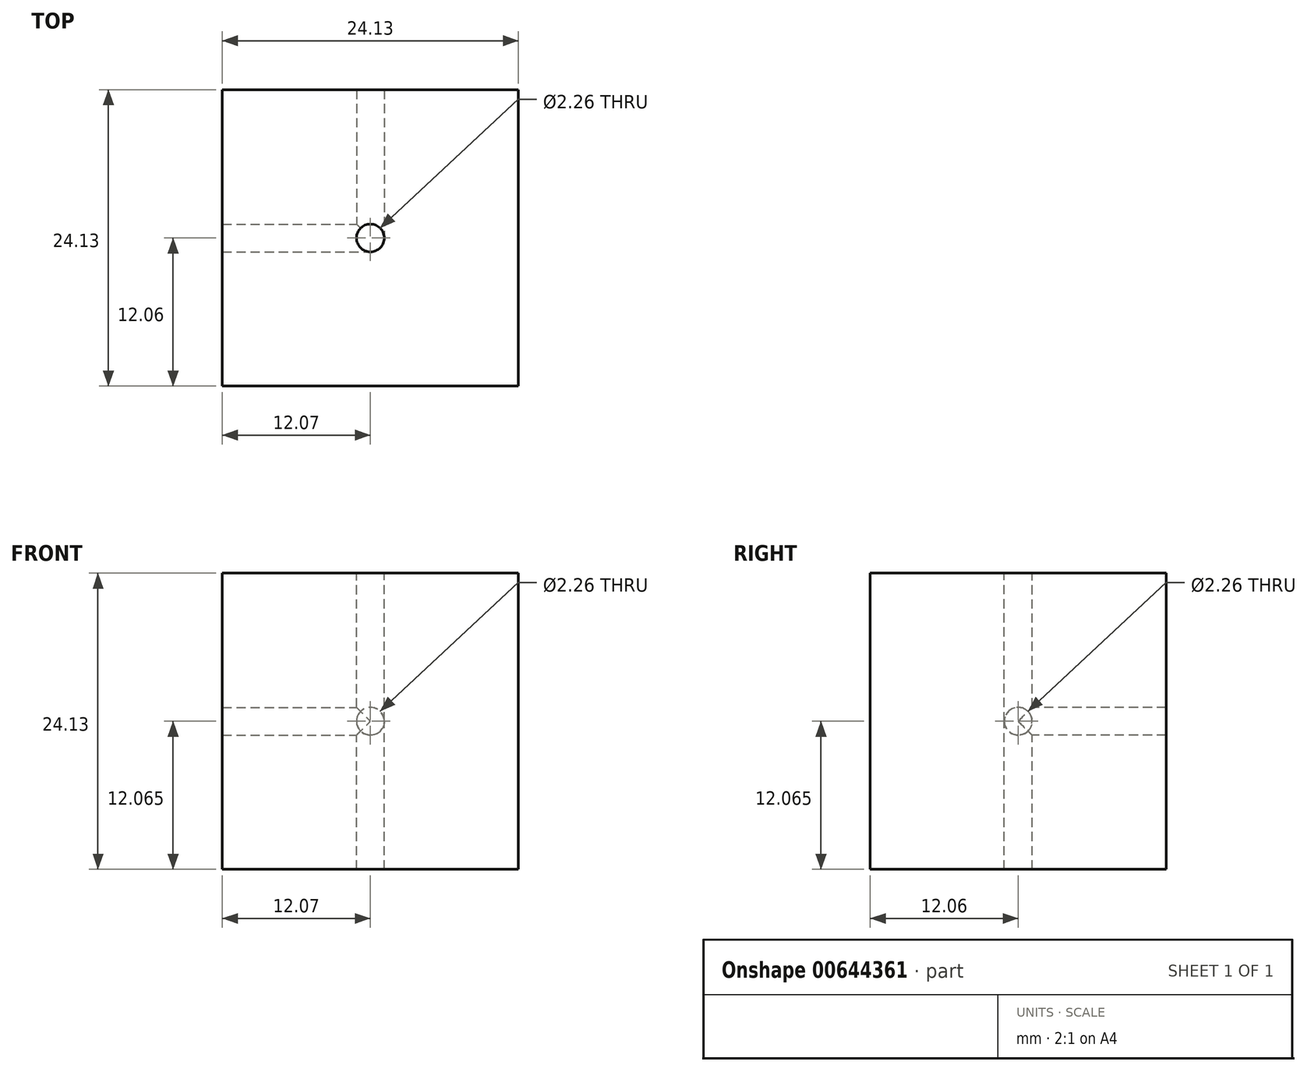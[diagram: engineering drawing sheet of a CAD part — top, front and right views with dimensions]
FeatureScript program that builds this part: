
annotation { "Feature Type Name" : "Feature", "Feature Type Description" : "" }
export const myFeature = defineFeature(function(context is Context, id is Id, definition is map)
    precondition{}
    {
        {
            var Q0;
            Q0=qCreatedBy(makeId("Top.planeOp"),FACE);
            var sketch = newSketch(context, id + "F0", { "sketchPlane" : qUnion([Q0])});
            skLineSegment(sketch, "E0.bottom", {"start": v(12.07, 12.07) * mm, "end": v(-12.07, 12.07) * mm});
            skLineSegment(sketch, "E0.top", {"start": v(12.07, -12.06) * mm, "end": v(-12.07, -12.06) * mm});
            skLineSegment(sketch, "E0.left", {"start": v(12.07, 12.07) * mm, "end": v(12.07, -12.06) * mm});
            skLineSegment(sketch, "E0.right", {"start": v(-12.07, 12.07) * mm, "end": v(-12.07, -12.06) * mm});
            skPoint(sketch, "E0.middle", {"position": v(0, 0) * mm});
            skSolve(sketch);
        }
        {
            var Q0;
            Q0=makeQuery(id+"F0.imprint","IMPRINT",FACE,{"disambiguationData":[TD([[makeQuery(id+"F0.imprint","IMPRINT",EDGE,{"derivedFrom":sQuery(id+"F0.wireOp",EDGE,"E0.bottom")}),1.0]])]});
            extrude(context, id + "F1", {"entities" : qUnion([Q0]), "depth" : 24.13 * mm, "offsetDistance" : 25.4 * mm});
        }
        {
            var Q0;
            Q0=makeQuery(id+"F1.opExtrude","CAP_FACE",FACE,{"disambiguationData":[OSD([sQuery(id+"F0.wireOp",EDGE,"E0.bottom"),sQuery(id+"F0.wireOp",EDGE,"E0.top"),sQuery(id+"F0.wireOp",EDGE,"E0.left"),sQuery(id+"F0.wireOp",EDGE,"E0.right")])],"isStart":false});
            var sketch = newSketch(context, id + "F2", { "sketchPlane" : qUnion([Q0])});
            skPoint(sketch, "E1", {"position": v(0, 0) * mm});
            skSolve(sketch);
        }
        {
            var Q0;
            Q0=sQuery(id+"F2.wireOp",VERTEX,"E1");
            var Q1;
            Q1=makeQuery(id+"F1.opExtrude","SWEPT_BODY",BODY,{"disambiguationData":[OSD([sQuery(id+"F0.wireOp",EDGE,"E0.bottom"),sQuery(id+"F0.wireOp",EDGE,"E0.top"),sQuery(id+"F0.wireOp",EDGE,"E0.left"),sQuery(id+"F0.wireOp",EDGE,"E0.right")])]});
            hole(context, id + "F3", {"style" : HoleStyle.SIMPLE, "endStyle" : HoleEndStyle.THROUGH, "standardTappedOrClearance" : lookupTablePath({ "standard" : "ANSI", "engagement" : "75%", "pitch" : "40 tpi", "size" : "#4", "type" : "Tapped" }), "standardBlindInLast" : lookupTablePath({ "standard" : "ANSI", "engagement" : "75%", "pitch" : "40 tpi", "size" : "#4", "type" : "Tapped" }), "holeDiameter" : 2.26 * mm, "majorDiameter" : 2.84 * mm, "showTappedDepth" : true, "tappedDepth" : 4.57 * mm, "tapClearance" : 3, "locations" : qUnion([Q0]), "scope" : qUnion([Q1])});
        }
        {
            var Q0;
            Q0=qCreatedBy(makeId("Front.planeOp"),FACE);
            var sketch = newSketch(context, id + "F4", { "sketchPlane" : qUnion([Q0])});
            skPoint(sketch, "E2", {"position": v(0, 12.07) * mm});
            skSolve(sketch);
        }
        {
            var Q0;
            Q0=sQuery(id+"F4.wireOp",VERTEX,"E2");
            var Q1;
            Q1=makeQuery(id+"F1.opExtrude","SWEPT_BODY",BODY,{"disambiguationData":[OSD([sQuery(id+"F0.wireOp",EDGE,"E0.bottom"),sQuery(id+"F0.wireOp",EDGE,"E0.top"),sQuery(id+"F0.wireOp",EDGE,"E0.left"),sQuery(id+"F0.wireOp",EDGE,"E0.right")])]});
            hole(context, id + "F5", {"style" : HoleStyle.SIMPLE, "endStyle" : HoleEndStyle.THROUGH, "standardTappedOrClearance" : lookupTablePath({ "standard" : "ANSI", "engagement" : "75%", "pitch" : "40 tpi", "size" : "#4", "type" : "Tapped" }), "standardBlindInLast" : lookupTablePath({ "standard" : "ANSI", "engagement" : "75%", "pitch" : "40 tpi", "size" : "#4", "type" : "Tapped" }), "holeDiameter" : 2.26 * mm, "majorDiameter" : 2.84 * mm, "showTappedDepth" : true, "tappedDepth" : 4.57 * mm, "tapClearance" : 3, "locations" : qUnion([Q0]), "scope" : qUnion([Q1])});
        }
        {
            var Q0;
            Q0=qCreatedBy(makeId("Right.planeOp"),FACE);
            var sketch = newSketch(context, id + "F6", { "sketchPlane" : qUnion([Q0])});
            skPoint(sketch, "E3", {"position": v(0, 12.07) * mm});
            skSolve(sketch);
        }
        {
            var Q0;
            Q0=sQuery(id+"F6.wireOp",VERTEX,"E3");
            var Q1;
            Q1=makeQuery(id+"F1.opExtrude","SWEPT_BODY",BODY,{"disambiguationData":[OSD([sQuery(id+"F0.wireOp",EDGE,"E0.bottom"),sQuery(id+"F0.wireOp",EDGE,"E0.top"),sQuery(id+"F0.wireOp",EDGE,"E0.left"),sQuery(id+"F0.wireOp",EDGE,"E0.right")])]});
            hole(context, id + "F7", {"style" : HoleStyle.SIMPLE, "endStyle" : HoleEndStyle.THROUGH, "standardTappedOrClearance" : lookupTablePath({ "standard" : "ANSI", "engagement" : "75%", "pitch" : "40 tpi", "size" : "#4", "type" : "Tapped" }), "standardBlindInLast" : lookupTablePath({ "standard" : "ANSI", "engagement" : "75%", "pitch" : "40 tpi", "size" : "#4", "type" : "Tapped" }), "holeDiameter" : 2.26 * mm, "majorDiameter" : 2.84 * mm, "showTappedDepth" : true, "tappedDepth" : 4.57 * mm, "tapClearance" : 3, "locations" : qUnion([Q0]), "scope" : qUnion([Q1])});
        }
    });
